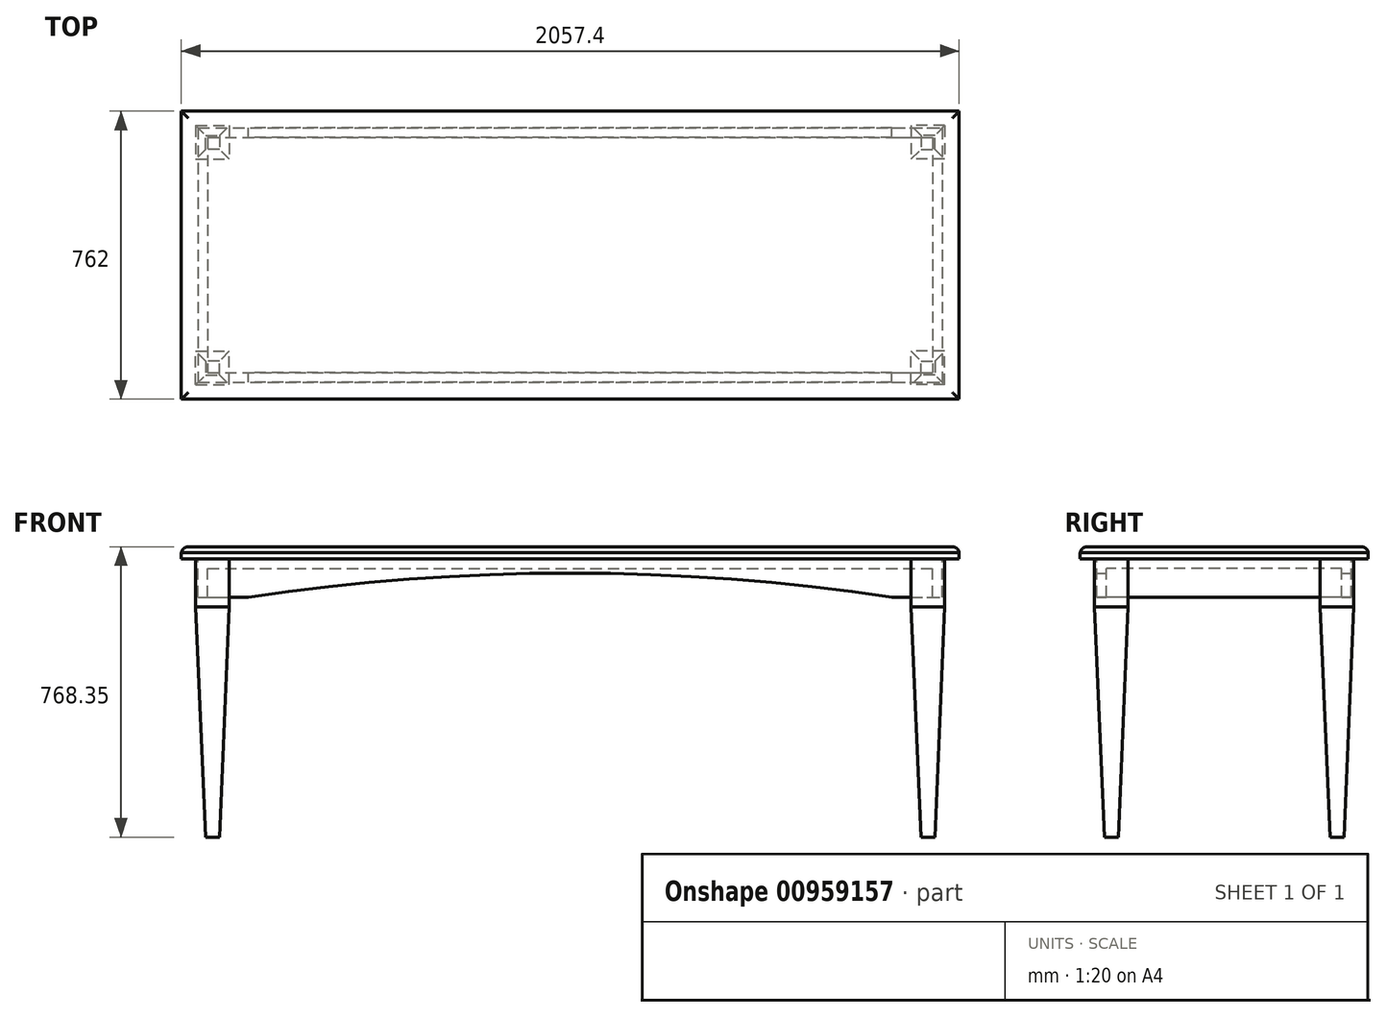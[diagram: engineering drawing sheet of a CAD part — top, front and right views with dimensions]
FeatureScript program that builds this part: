
annotation { "Feature Type Name" : "Feature", "Feature Type Description" : "" }
export const myFeature = defineFeature(function(context is Context, id is Id, definition is map)
    precondition{}
    {
        {
            var Q0;
            Q0=qCreatedBy(makeId("Top.planeOp"),FACE);
            var sketch = newSketch(context, id + "F0", { "sketchPlane" : qUnion([Q0])});
            skLineSegment(sketch, "E0.bottom", {"start": v(-1028.7, 381) * mm, "end": v(1028.7, 381) * mm});
            skLineSegment(sketch, "E0.top", {"start": v(-1028.7, -381) * mm, "end": v(1028.7, -381) * mm});
            skLineSegment(sketch, "E0.left", {"start": v(-1028.7, 381) * mm, "end": v(-1028.7, -381) * mm});
            skLineSegment(sketch, "E0.right", {"start": v(1028.7, 381) * mm, "end": v(1028.7, -381) * mm});
            skPoint(sketch, "E0.middle", {"position": v(0, 0) * mm});
            skSolve(sketch);
        }
        {
            var Q0;
            Q0 = qSketchRegion(id + "F0", true);
            extrude(context, id + "F1", {"entities" : qUnion([Q0]), "depth" : 15.88 * mm, "offsetDistance" : 25.4 * mm});
        }
        {
            var Q0;
            Q0=makeQuery(id+"F1.opExtrude","CAP_FACE",FACE,{"disambiguationData":[OSD([sQuery(id+"F0.wireOp",EDGE,"E0.bottom"),sQuery(id+"F0.wireOp",EDGE,"E0.top"),sQuery(id+"F0.wireOp",EDGE,"E0.left"),sQuery(id+"F0.wireOp",EDGE,"E0.right")])],"isStart":false});
            var sketch = newSketch(context, id + "F2", { "sketchPlane" : qUnion([Q0])});
            skLineSegment(sketch, "E1.bottom", {"start": v(-1028.7, 381) * mm, "end": v(1028.7, 381) * mm});
            skLineSegment(sketch, "E1.top", {"start": v(-1028.7, -381) * mm, "end": v(1028.7, -381) * mm});
            skLineSegment(sketch, "E1.left", {"start": v(-1028.7, 381) * mm, "end": v(-1028.7, -381) * mm});
            skLineSegment(sketch, "E1.right", {"start": v(1028.7, 381) * mm, "end": v(1028.7, -381) * mm});
            skPoint(sketch, "E1.middle", {"position": v(0, 0) * mm});
            skSolve(sketch);
        }
        {
            var Q0;
            Q0 = qSketchRegion(id + "F2", true);
            extrude(context, id + "F3", {"entities" : qUnion([Q0]), "depth" : 15.88 * mm, "offsetDistance" : 25.4 * mm});
        }
        {
            var Q0;
            Q0=makeQuery(id+"F3.opExtrude","CAP_EDGE",EDGE,{"disambiguationData":[OSD([sQuery(id+"F2.wireOp",EDGE,"E1.top")])],"isStart":false});
            var Q1;
            Q1=makeQuery(id+"F3.opExtrude","CAP_EDGE",EDGE,{"disambiguationData":[OSD([sQuery(id+"F2.wireOp",EDGE,"E1.left")])],"isStart":false});
            var Q2;
            Q2=makeQuery(id+"F3.opExtrude","CAP_EDGE",EDGE,{"disambiguationData":[OSD([sQuery(id+"F2.wireOp",EDGE,"E1.right")])],"isStart":false});
            var Q3;
            Q3=makeQuery(id+"F3.opExtrude","CAP_EDGE",EDGE,{"disambiguationData":[OSD([sQuery(id+"F2.wireOp",EDGE,"E1.bottom")])],"isStart":false});
            fillet(context, id + "F4", {"entities" : qUnion([Q0, Q1, Q2, Q3]), "radius" : 19.05 * mm, "tangentPropagation" : true, "allowEdgeOverflow" : false});
        }
        {
            var Q0;
            Q0=makeQuery(id+"F1.opExtrude","CAP_FACE",FACE,{"disambiguationData":[OSD([sQuery(id+"F0.wireOp",EDGE,"E0.bottom"),sQuery(id+"F0.wireOp",EDGE,"E0.top"),sQuery(id+"F0.wireOp",EDGE,"E0.left"),sQuery(id+"F0.wireOp",EDGE,"E0.right")])],"isStart":true});
            var sketch = newSketch(context, id + "F5", { "sketchPlane" : qUnion([Q0])});
            skLineSegment(sketch, "E2.bottom", {"start": v(-1028.7, -381) * mm, "end": v(1028.7, -381) * mm});
            skLineSegment(sketch, "E2.top", {"start": v(-1028.7, 381) * mm, "end": v(1028.7, 381) * mm});
            skLineSegment(sketch, "E2.left", {"start": v(-1028.7, -381) * mm, "end": v(-1028.7, 381) * mm});
            skLineSegment(sketch, "E2.right", {"start": v(1028.7, -381) * mm, "end": v(1028.7, 381) * mm});
            skPoint(sketch, "E2.middle", {"position": v(0, 0) * mm});
            skLineSegment(sketch, "E3.0", {"start": v(-990.6, -342.9) * mm, "end": v(-990.6, 342.9) * mm});
            skLineSegment(sketch, "E3.1", {"start": v(-990.6, -342.9) * mm, "end": v(990.6, -342.9) * mm});
            skLineSegment(sketch, "E3.2", {"start": v(990.6, -342.9) * mm, "end": v(990.6, 342.9) * mm});
            skLineSegment(sketch, "E3.3", {"start": v(-990.6, 342.9) * mm, "end": v(990.6, 342.9) * mm});
            skLineSegment(sketch, "E4.0", {"start": v(-984.25, 336.55) * mm, "end": v(984.25, 336.55) * mm});
            skLineSegment(sketch, "E4.1", {"start": v(-984.25, -336.55) * mm, "end": v(-984.25, 336.55) * mm});
            skLineSegment(sketch, "E4.2", {"start": v(-984.25, -336.55) * mm, "end": v(984.25, -336.55) * mm});
            skLineSegment(sketch, "E4.3", {"start": v(984.25, -336.55) * mm, "end": v(984.25, 336.55) * mm});
            skLineSegment(sketch, "E5.bottom", {"start": v(-990.6, 342.9) * mm, "end": v(-901.7, 342.9) * mm});
            skLineSegment(sketch, "E5.top", {"start": v(-990.6, 254) * mm, "end": v(-901.7, 254) * mm});
            skLineSegment(sketch, "E5.left", {"start": v(-990.6, 342.9) * mm, "end": v(-990.6, 254) * mm});
            skLineSegment(sketch, "E5.right", {"start": v(-901.7, 342.9) * mm, "end": v(-901.7, 254) * mm});
            skLineSegment(sketch, "E6", {"start": v(-775.87, 0) * mm, "end": v(783.48, 0) * mm, "construction": true});
            skLineSegment(sketch, "E7", {"start": v(0, 524.15) * mm, "end": v(0, -552.6) * mm, "construction": true});
            skLineSegment(sketch, "E8.MirrorCS", {"start": v(-901.7, -342.9) * mm, "end": v(-901.7, -254) * mm});
            skLineSegment(sketch, "E9.MirrorCS", {"start": v(-990.6, -342.9) * mm, "end": v(-901.7, -342.9) * mm});
            skLineSegment(sketch, "E10.MirrorCS", {"start": v(-990.6, -342.9) * mm, "end": v(-990.6, -254) * mm});
            skLineSegment(sketch, "E11.MirrorCS", {"start": v(-990.6, -254) * mm, "end": v(-901.7, -254) * mm});
            skSolve(sketch);
        }
        {
            var Q0;
            {var subQ0=sQuery(id+"F5.wireOp",EDGE,"E4.3");Q0=makeQuery(id+"F5.imprint","IMPRINT",FACE,{"disambiguationData":[TD([[makeQuery(id+"F5.imprint","IMPRINT",EDGE,{"derivedFrom":subQ0}),1.0]])]});}
            var sketch = newSketch(context, id + "F6", { "sketchPlane" : qUnion([Q0])});
            skLineSegment(sketch, "E12.0", {"start": v(-990.6, 342.9) * mm, "end": v(-901.7, 342.9) * mm});
            skLineSegment(sketch, "E13.0", {"start": v(-901.7, 342.9) * mm, "end": v(-901.7, 254) * mm});
            skLineSegment(sketch, "E14.0", {"start": v(-990.6, 342.9) * mm, "end": v(-990.6, 254) * mm});
            skLineSegment(sketch, "E15.0", {"start": v(-990.6, 254) * mm, "end": v(-901.7, 254) * mm});
            skLineSegment(sketch, "E16.0", {"start": v(-990.6, -254) * mm, "end": v(-901.7, -254) * mm});
            skLineSegment(sketch, "E17.0", {"start": v(-901.7, -342.9) * mm, "end": v(-901.7, -254) * mm});
            skLineSegment(sketch, "E18.0", {"start": v(-990.6, -342.9) * mm, "end": v(-901.7, -342.9) * mm});
            skLineSegment(sketch, "E19.0", {"start": v(-990.6, -342.9) * mm, "end": v(-990.6, -254) * mm});
            skSolve(sketch);
        }
        {
            var Q0;
            Q0 = qSketchRegion(id + "F6", true);
            extrude(context, id + "F7", {"entities" : qUnion([Q0]), "depth" : 127 * mm, "offsetDistance" : 25.4 * mm});
        }
        {
            var Q0;
            Q0=makeQuery(id+"F7.opExtrude","SWEPT_BODY",BODY,{"disambiguationData":[OSD([sQuery(id+"F6.wireOp",EDGE,"E12.0"),sQuery(id+"F6.wireOp",EDGE,"E13.0"),sQuery(id+"F6.wireOp",EDGE,"E14.0"),sQuery(id+"F6.wireOp",EDGE,"E15.0")])]});
            var Q1;
            Q1=makeQuery(id+"F7.opExtrude","SWEPT_BODY",BODY,{"disambiguationData":[OSD([sQuery(id+"F6.wireOp",EDGE,"E16.0"),sQuery(id+"F6.wireOp",EDGE,"E17.0"),sQuery(id+"F6.wireOp",EDGE,"E18.0"),sQuery(id+"F6.wireOp",EDGE,"E19.0")])]});
            var Q2;
            Q2=qCreatedBy(makeId("Right.planeOp"),FACE);
            mirror(context, id + "F8", {"operationType" : NewBodyOperationType.ADD, "entities" : qUnion([Q0, Q1]), "mirrorPlane" : qUnion([Q2])});
        }
        {
            var Q0;
            {var subQ0=sQuery(id+"F5.wireOp",EDGE,"E4.3");Q0=makeQuery(id+"F5.imprint","IMPRINT",FACE,{"disambiguationData":[TD([[makeQuery(id+"F5.imprint","IMPRINT",EDGE,{"derivedFrom":subQ0}),1.0]])]});}
            var sketch = newSketch(context, id + "F9", { "sketchPlane" : qUnion([Q0])});
            skLineSegment(sketch, "E20.0", {"start": v(-984.25, 336.55) * mm, "end": v(984.25, 336.55) * mm});
            skLineSegment(sketch, "E21.0", {"start": v(-984.25, -336.55) * mm, "end": v(-984.25, 336.55) * mm});
            skLineSegment(sketch, "E22.0", {"start": v(-984.25, -336.55) * mm, "end": v(984.25, -336.55) * mm});
            skLineSegment(sketch, "E23.0", {"start": v(984.25, -336.55) * mm, "end": v(984.25, 336.55) * mm});
            skSolve(sketch);
        }
        {
            var Q0;
            Q0 = qSketchRegion(id + "F9", true);
            extrude(context, id + "F10", {"entities" : qUnion([Q0]), "depth" : 101.6 * mm, "offsetDistance" : 25.4 * mm});
        }
        {
            var Q0;
            Q0=makeQuery(id+"F10.opExtrude","CAP_FACE",FACE,{"disambiguationData":[OSD([sQuery(id+"F9.wireOp",EDGE,"E20.0"),sQuery(id+"F9.wireOp",EDGE,"E21.0"),sQuery(id+"F9.wireOp",EDGE,"E22.0"),sQuery(id+"F9.wireOp",EDGE,"E23.0")])],"isStart":false});
            var Q1;
            Q1=makeQuery(id+"F10.opExtrude","SWEPT_BODY",BODY,{"disambiguationData":[OSD([sQuery(id+"F9.wireOp",EDGE,"E20.0"),sQuery(id+"F9.wireOp",EDGE,"E21.0"),sQuery(id+"F9.wireOp",EDGE,"E22.0"),sQuery(id+"F9.wireOp",EDGE,"E23.0")])]});
            shell(context, id + "F11", {"entities" : qUnion([Q0]), "parts" : qUnion([Q1]), "thickness" : 25.4 * mm});
        }
        {
            var Q0;
            Q0=makeQuery(id+"F7.opExtrude","CAP_FACE",FACE,{"disambiguationData":[OSD([sQuery(id+"F6.wireOp",EDGE,"E12.0"),sQuery(id+"F6.wireOp",EDGE,"E13.0"),sQuery(id+"F6.wireOp",EDGE,"E14.0"),sQuery(id+"F6.wireOp",EDGE,"E15.0")])],"isStart":false});
            var sketch = newSketch(context, id + "F12", { "sketchPlane" : qUnion([Q0])});
            skLineSegment(sketch, "E24.0.0", {"start": v(-990.6, 342.9) * mm, "end": v(-990.6, 254) * mm});
            skLineSegment(sketch, "E24.0.1", {"start": v(-990.6, 254) * mm, "end": v(-901.7, 254) * mm});
            skLineSegment(sketch, "E24.0.2", {"start": v(-901.7, 254) * mm, "end": v(-901.7, 342.9) * mm});
            skLineSegment(sketch, "E24.0.3", {"start": v(-901.7, 342.9) * mm, "end": v(-990.6, 342.9) * mm});
            skSolve(sketch);
        }
        {
            var Q0;
            Q0 = qSketchRegion(id + "F12", true);
            extrude(context, id + "F13", {"entities" : qUnion([Q0]), "depth" : 609.6 * mm, "offsetDistance" : 25.4 * mm, "hasDraft" : true, "draftAngle" : 2.5 * degree, "draftPullDirection" : true});
        }
        {
            var Q0;
            Q0=makeQuery(id+"F13.opExtrude","SWEPT_BODY",BODY,{"disambiguationData":[OSD([sQuery(id+"F12.wireOp",EDGE,"E24.0.0"),sQuery(id+"F12.wireOp",EDGE,"E24.0.1"),sQuery(id+"F12.wireOp",EDGE,"E24.0.2"),sQuery(id+"F12.wireOp",EDGE,"E24.0.3")])]});
            var Q1;
            Q1=qCreatedBy(makeId("Front.planeOp"),FACE);
            mirror(context, id + "F14", {"entities" : qUnion([Q0]), "mirrorPlane" : qUnion([Q1])});
        }
        {
            var Q0;
            Q0=makeQuery(id+"F13.opExtrude","SWEPT_BODY",BODY,{"disambiguationData":[OSD([sQuery(id+"F12.wireOp",EDGE,"E24.0.0"),sQuery(id+"F12.wireOp",EDGE,"E24.0.1"),sQuery(id+"F12.wireOp",EDGE,"E24.0.2"),sQuery(id+"F12.wireOp",EDGE,"E24.0.3")])]});
            var Q1;
            Q1=makeQuery(id+"F14.opPattern","COPY",BODY,{"derivedFrom":makeQuery(id+"F13.opExtrude","SWEPT_BODY",BODY,{"disambiguationData":[OSD([sQuery(id+"F12.wireOp",EDGE,"E24.0.0"),sQuery(id+"F12.wireOp",EDGE,"E24.0.1"),sQuery(id+"F12.wireOp",EDGE,"E24.0.2"),sQuery(id+"F12.wireOp",EDGE,"E24.0.3")])]}),"instanceName":"1"});
            var Q2;
            Q2=qCreatedBy(makeId("Right.planeOp"),FACE);
            mirror(context, id + "F15", {"operationType" : NewBodyOperationType.ADD, "entities" : qUnion([Q0, Q1]), "mirrorPlane" : qUnion([Q2])});
        }
        {
            var Q0;
            Q0=qCreatedBy(makeId("Front.planeOp"),FACE);
            var sketch = newSketch(context, id + "F16", { "sketchPlane" : qUnion([Q0])});
            skLineSegment(sketch, "E25.0.0", {"start": v(984.25, 0) * mm, "end": v(-984.25, 0) * mm, "construction": true});
            skLineSegment(sketch, "E25.0.1", {"start": v(-984.25, 0) * mm, "end": v(-984.25, -101.6) * mm, "construction": true});
            skLineSegment(sketch, "E25.0.2", {"start": v(-984.25, -101.6) * mm, "end": v(984.25, -101.6) * mm, "construction": true});
            skLineSegment(sketch, "E25.0.3", {"start": v(984.25, -101.6) * mm, "end": v(984.25, 0) * mm, "construction": true});
            skLineSegment(sketch, "E26.0.0", {"start": v(-901.7, 0) * mm, "end": v(-990.6, 0) * mm, "construction": true});
            skLineSegment(sketch, "E26.0.1", {"start": v(-990.6, 0) * mm, "end": v(-990.6, -127) * mm, "construction": true});
            skLineSegment(sketch, "E26.0.2", {"start": v(-990.6, -127) * mm, "end": v(-901.7, -127) * mm, "construction": true});
            skLineSegment(sketch, "E26.0.3", {"start": v(-901.7, -127) * mm, "end": v(-901.7, 0) * mm, "construction": true});
            skLineSegment(sketch, "E27", {"start": v(-901.7, -101.6) * mm, "end": v(-850.9, -101.6) * mm, "construction": true});
            skArc(sketch, "E28", {"start": v(850.9, -101.6) * mm, "mid": v(0, -38.1) * mm, "end": v(-850.9, -101.6) * mm});
            skPoint(sketch, "E29", {"position": v(0, -38.1) * mm});
            skLineSegment(sketch, "E30.bottom", {"start": v(-381, 129.72) * mm, "end": v(381, 129.72) * mm, "construction": true});
            skLineSegment(sketch, "E30.top", {"start": v(-381, -792.5) * mm, "end": v(381, -792.5) * mm, "construction": true});
            skLineSegment(sketch, "E30.left", {"start": v(-381, 129.72) * mm, "end": v(-381, -792.5) * mm, "construction": true});
            skLineSegment(sketch, "E30.right", {"start": v(381, 129.72) * mm, "end": v(381, -792.5) * mm, "construction": true});
            skPoint(sketch, "E30.middle", {"position": v(0, -331.4) * mm});
            skPoint(sketch, "E31", {"position": v(-381, -50.77) * mm});
            skLineSegment(sketch, "E32", {"start": v(-901.7, -101.6) * mm, "end": v(-901.7, -354.54) * mm});
            skLineSegment(sketch, "E33.bottom", {"start": v(-850.9, -101.6) * mm, "end": v(850.9, -101.6) * mm});
            skLineSegment(sketch, "E33.top", {"start": v(-850.9, -346.83) * mm, "end": v(850.9, -346.83) * mm});
            skLineSegment(sketch, "E33.left", {"start": v(-850.9, -101.6) * mm, "end": v(-850.9, -346.83) * mm});
            skLineSegment(sketch, "E33.right", {"start": v(850.9, -101.6) * mm, "end": v(850.9, -346.83) * mm});
            skSolve(sketch);
        }
        {
            var Q0;
            Q0 = qSketchRegion(id + "F16", true);
            extrude(context, id + "F17", {"entities" : qUnion([Q0]), "operationType" : NewBodyOperationType.REMOVE, "depth" : 914.4 * mm, "offsetDistance" : 25.4 * mm, "hasSecondDirection" : true, "secondDirectionOppositeDirection" : true, "secondDirectionDepth" : 914.4 * mm});
        }
    });
